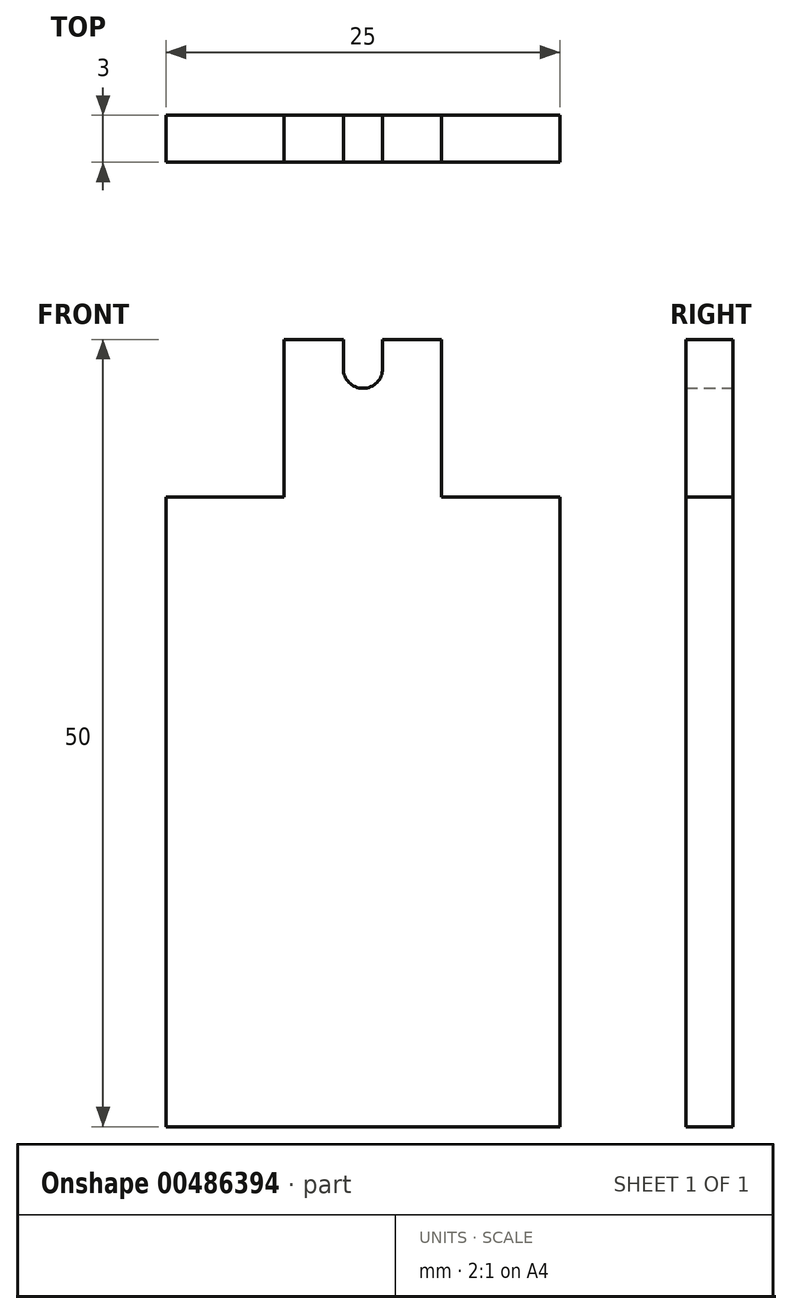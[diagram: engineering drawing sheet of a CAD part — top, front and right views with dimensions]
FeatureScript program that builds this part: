
annotation { "Feature Type Name" : "Feature", "Feature Type Description" : "" }
export const myFeature = defineFeature(function(context is Context, id is Id, definition is map)
    precondition{}
    {
        {
            var Q0;
            Q0=qCreatedBy(makeId("Front.planeOp"),FACE);
            var sketch = newSketch(context, id + "F0", { "sketchPlane" : qUnion([Q0])});
            skLineSegment(sketch, "E0.bottom", {"start": v(0, 0) * mm, "end": v(25, 0) * mm});
            skLineSegment(sketch, "E0.top", {"start": v(0, 40) * mm, "end": v(7.5, 40) * mm});
            skLineSegment(sketch, "E0.left", {"start": v(0, 0) * mm, "end": v(0, 40) * mm});
            skLineSegment(sketch, "E0.right", {"start": v(25, 0) * mm, "end": v(25, 40) * mm});
            skLineSegment(sketch, "E1.top", {"start": v(7.5, 50) * mm, "end": v(11.25, 50) * mm});
            skLineSegment(sketch, "E1.left", {"start": v(7.5, 40) * mm, "end": v(7.5, 50) * mm});
            skLineSegment(sketch, "E1.right", {"start": v(17.5, 40) * mm, "end": v(17.5, 50) * mm});
            skLineSegment(sketch, "E2.trimOffspring", {"start": v(17.5, 40) * mm, "end": v(25, 40) * mm});
            skLineSegment(sketch, "E3", {"start": v(11.25, 50) * mm, "end": v(11.25, 48.15) * mm});
            skLineSegment(sketch, "E4", {"start": v(11.25, 48.15) * mm, "end": v(13.75, 48.15) * mm, "construction": true});
            skLineSegment(sketch, "E5", {"start": v(13.75, 48.15) * mm, "end": v(13.75, 50) * mm});
            skArc(sketch, "E6", {"start": v(13.75, 48.15) * mm, "mid": v(12.5, 46.9) * mm, "end": v(11.25, 48.15) * mm});
            skLineSegment(sketch, "E7", {"start": v(12.5, 48.15) * mm, "end": v(12.5, 46.9) * mm, "construction": true});
            skLineSegment(sketch, "E8.trimOffspring", {"start": v(13.75, 50) * mm, "end": v(17.5, 50) * mm});
            skPoint(sketch, "E9", {"position": v(12.5, 5) * mm});
            skSolve(sketch);
        }
        {
            var Q0;
            Q0=makeQuery(id+"F0.imprint","IMPRINT",FACE,{"disambiguationData":[TD([[makeQuery(id+"F0.imprint","IMPRINT",EDGE,{"derivedFrom":sQuery(id+"F0.wireOp",EDGE,"E0.bottom")}),1.0]])]});
            extrude(context, id + "F1", {"entities" : qUnion([Q0]), "depth" : 3 * mm});
        }
    });
